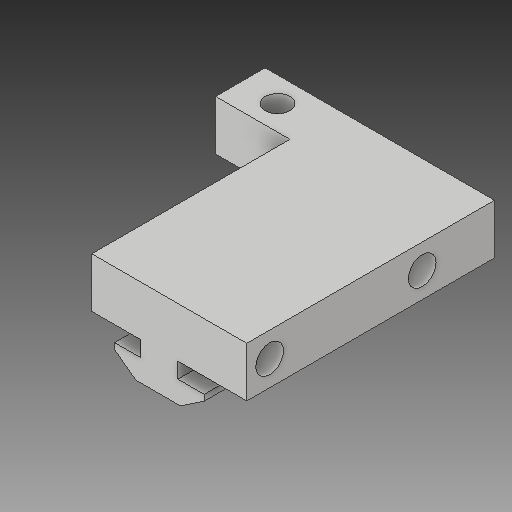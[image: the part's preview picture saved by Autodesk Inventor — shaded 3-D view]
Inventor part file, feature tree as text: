
AUTODESK INVENTOR PART (.ipt)
format: ipt  version: 2019 (Build 230136000, 136)  size: 181,248 bytes
history: native  units: in
note: dims shown in document units (in); Inventor stores cm internally (conversion verified against a paired STEP export)
features: sketch x6, projected_geometry x5, extrude x4, hole x2
ambient origin geometry x8: Origin, YZ Plane, XZ Plane, XY Plane, X Axis, Y Axis, Z Axis, Center Point
bodies: Solid1 (feature_tree)
feature tree (17):
  extrude  "Extrusion1"  Depth=0.0787in
  extrude  "Extrusion6"  Depth=0.115in
  extrude  "Extrusion9"  Depth=0.03in
  hole  "Hole11"  [1 undecoded]
  extrude  "Extrusion10"  Depth=0.1325in
  hole  "Hole12"  [1 undecoded]
  sketch  "Sketch1"  dims[d0=0.6693in d2=0.1969in d3=0.0787in]
  sketch  "Sketch14"  dims[d6=0.4524in d7=0.115in]
  projected_geometry  "Projected Loop4"
  sketch  "Sketch17"  dims[d8=0.225in d9=0.2221in d11=0.03in]
  projected_geometry  "Projected Loop7"
  sketch  "Sketch19"  dims[d12=0.03in d13=1.0in d14=0.0in]
  projected_geometry  "Projected Loop9"
  sketch  "Sketch20"  dims[d78=0.215in d88=0.1325in]
  projected_geometry  "Projected Loop10"
  sketch  "Sketch21"  dims[d89=0.1325in d161=0.25in d162=0.375in d163=0.0in d175=0.25in d176=0.055in d177=0.0in d190=0.125in d191=0.75in d192=0.375in d193=0.25in d194=0.5635in d195=1.0in d196=0.8108in d197=0.25in d198=0.0in d199=1.25in d200=0.77in d201=0.365in d202=0.125in d203=0.125in d204=0.14in d205=0.75in d206=0.375in d207=0.25in d208=0.5635in d209=1.0in d210=0.8108in d71=1.0in d72=1.0in d112=1.0in d113=1.0in]
  projected_geometry  "Projected Loop11"
note: 2 required parameter values undecoded (feature->parameter linkage not recoverable at this tier; creation-order binding heuristic only, values carry confidence <= 0.55)
